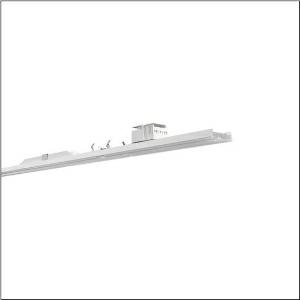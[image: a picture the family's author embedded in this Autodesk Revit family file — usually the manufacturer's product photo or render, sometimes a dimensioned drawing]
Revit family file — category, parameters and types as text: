
# Revit family: licross_r__11_recessed_mo_51tl18dn485f_a554
name_source: partatom
category: Lighting Fixtures
units: mm (PartAtom-declared; Revit-internal decimal feet)

## family parameters
Cut with Voids When Loaded = No
Host = Face
Light Source = No
Part Type = Normal
Room Calculation Point = No
Round Connector Dimension = Use Diameter
Shared = No

## types (1)
- --- (1 x LED, 8910 lm, 55.4 W, 4000K)
    Apparent Load = 55 VA
    CIE Flux Codes = 83 96 99 100 100
    Color Rendering = 80
    Color Temperature = 4000K
    Default Elevation = 1800 mm
    Description = Licross® 11 Recessed MOluminaire insert, length: 1.500mm, width: 66mm, height: 67mm, LED rated luminous flux: 8.910lm, light colour: 840, control gear: DALI 2, control gear: ECG DALI, with plug, 5-pole, with phase selection, mains connection: 220..240V, AC, 50/60Hz, halogen-free wiring, primary optical cover: cover, of PMMA, light emission: direct distribution, protection rating (complete): IP40, insulation class (complete): insulation class I (protective earthing), certification: CE, ENEC, VDE, protection symbol: D if used in an environment without relevant dust loads with corresponding accessories, permissible ambient temperature for indoor applications: -25..+40°C, reducing of maximum allowable ambient temperature of 5°C with ceiling mounting, corresponds to IFS (International Featured Standards) requirements for safety and quality in the food industry, packaging unit: 1 piece
    Height = 58 mm
    Lamp = 1 x LED
    Lamp Light Flux = 8910 lm
    Lamp Power = 55.4 W
    Lamp count = 1
    Length = 1500 mm
    Luminous efficacy = 161 lm/W
    Manufacturer = Siteco
    ModVariant = No
    Model = 51TL18DN485F
    Mounting Place = Ceiling
    Mounting Type = Pendant
    Number of Poles = 1
    OnlyDefault = Yes
    Power Factor = 1
    Product Name = Licross® 11 Recessed MO
    Product group = luminaire insert
    ProductGroupID = 902
    Protection Class = Protection class I
    Protection Degree = IP 40
    RLX_Detail_Level = 1
    RlxData = <blob elided: 22057 chars, md5=981758b0>
    Socket = socket
    Standby Power = 0 W
    System Light Flux = 8910 lm
    System Power = 55 W
    Type Comments = factory setting: luminous flux: 100 % | dim-lin: 254 | 365 mA
    Type Image = l_1266722.jpg
    URL = http://relux.com
    VarID = @adj_138617
    Voltage = 0 V
    Weight = 0.00 kg
    Width = 66 mm

## geometry (parser evidence)
native form markers: Blend x4, Sweep x10
no freeform markers — native parametric forms only
